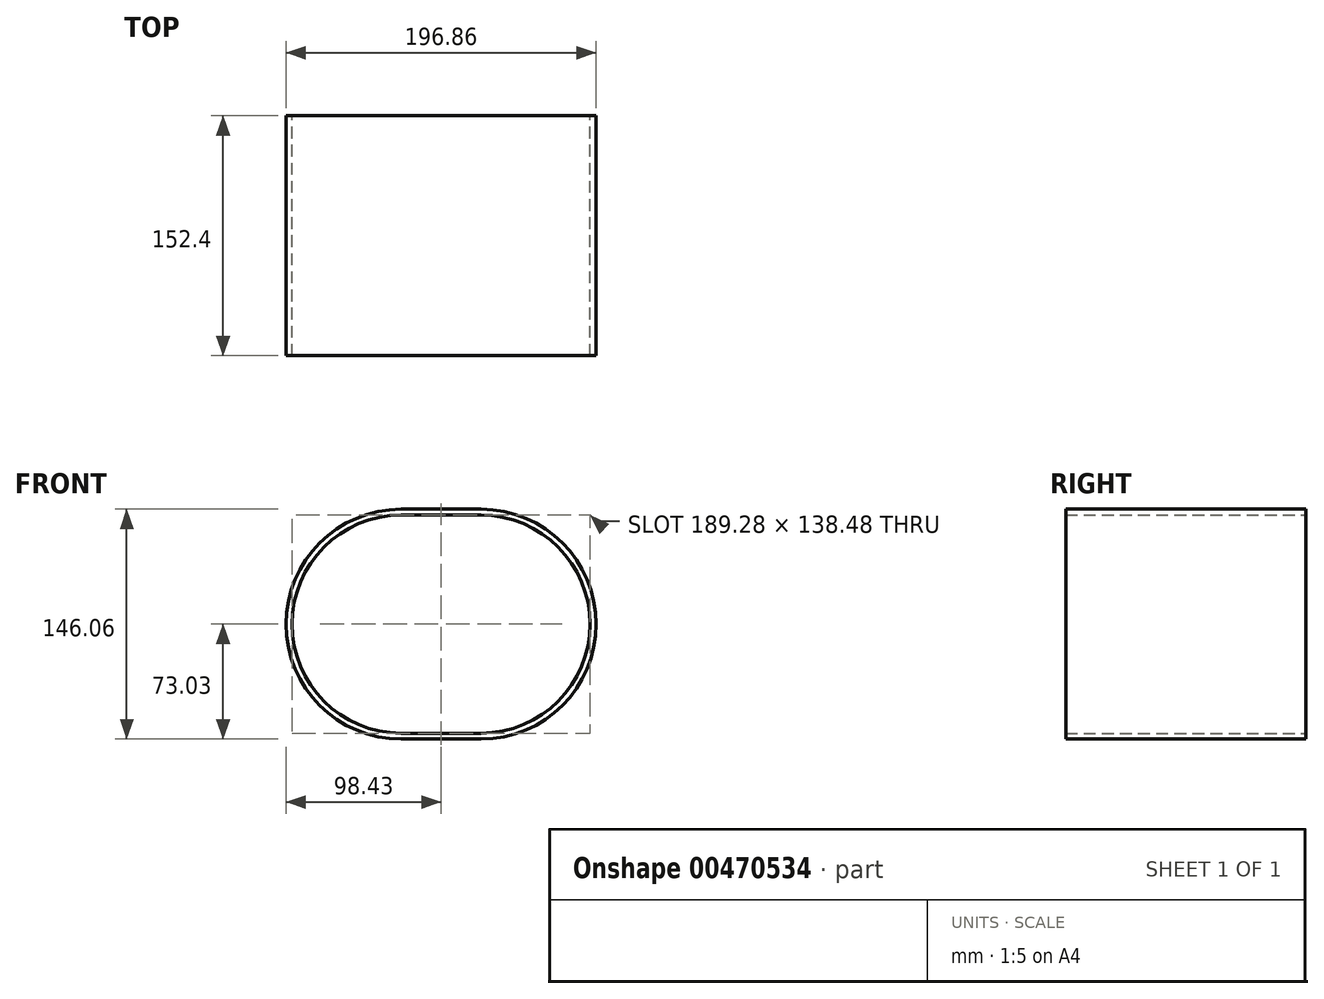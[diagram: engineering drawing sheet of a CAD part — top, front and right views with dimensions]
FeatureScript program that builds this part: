
annotation { "Feature Type Name" : "Feature", "Feature Type Description" : "" }
export const myFeature = defineFeature(function(context is Context, id is Id, definition is map)
    precondition{}
    {
        {
            var Q0;
            Q0=qCreatedBy(makeId("Front.planeOp"),FACE);
            var sketch = newSketch(context, id + "F0", { "sketchPlane" : qUnion([Q0])});
            skArc(sketch, "E0", {"start": v(0, -73.03) * mm, "mid": v(73.03, 0) * mm, "end": v(0, 73.03) * mm});
            skLineSegment(sketch, "E1", {"start": v(0, 73.03) * mm, "end": v(-25.4, 73.03) * mm});
            skLineSegment(sketch, "E2", {"start": v(0, -73.03) * mm, "end": v(-25.4, -73.03) * mm});
            skLineSegment(sketch, "E3", {"start": v(-25.4, 73.03) * mm, "end": v(-25.4, -73.03) * mm});
            skLineSegment(sketch, "E4.MirrorCS", {"start": v(-50.8, -73.03) * mm, "end": v(-25.4, -73.03) * mm});
            skLineSegment(sketch, "E5.MirrorCS", {"start": v(-50.8, 73.03) * mm, "end": v(-25.4, 73.03) * mm});
            skArc(sketch, "E6.MirrorCS", {"start": v(-50.8, -73.03) * mm, "mid": v(-123.83, 0) * mm, "end": v(-50.8, 73.03) * mm});
            skLineSegment(sketch, "E7", {"start": v(-25.4, 0) * mm, "end": v(-25.4, 76.2) * mm});
            skLineSegment(sketch, "E8", {"start": v(-50.8, 73.03) * mm, "end": v(-50.8, 76.2) * mm});
            skLineSegment(sketch, "E9", {"start": v(-50.8, -73.03) * mm, "end": v(-50.8, -86.12) * mm});
            skArc(sketch, "E10", {"start": v(-25.4, -64.41) * mm, "mid": v(69.24, 0) * mm, "end": v(-25.4, 64.41) * mm});
            skCircle(sketch, "E11", {"center": v(-50.8, 0) * mm, "radius": 69.24 * mm});
            skLineSegment(sketch, "E12", {"start": v(-50.8, 69.24) * mm, "end": v(0, 69.24) * mm});
            skLineSegment(sketch, "E13", {"start": v(-50.8, -69.24) * mm, "end": v(0, -69.24) * mm});
            skSolve(sketch);
        }
        {
            var Q0;
            {var subQ6=sQuery(id+"F0.wireOp",EDGE,"E4.MirrorCS");Q0=makeQuery(id+"F0.imprint","IMPRINT",FACE,{"disambiguationData":[TD([[makeQuery(id+"F0.imprint","IMPRINT",EDGE,{"derivedFrom":subQ6}),1.0]])]});}
            var Q1;
            Q1=makeQuery(id+"F0.imprint","IMPRINT",FACE,{"disambiguationData":[TD([[makeQuery(id+"F0.imprint","IMPRINT",EDGE,{"derivedFrom":sQuery(id+"F0.wireOp",EDGE,"E0")}),1.0]])]});
            extrude(context, id + "F1", {"entities" : qUnion([Q0, Q1]), "depth" : 152.4 * mm});
        }
    });
